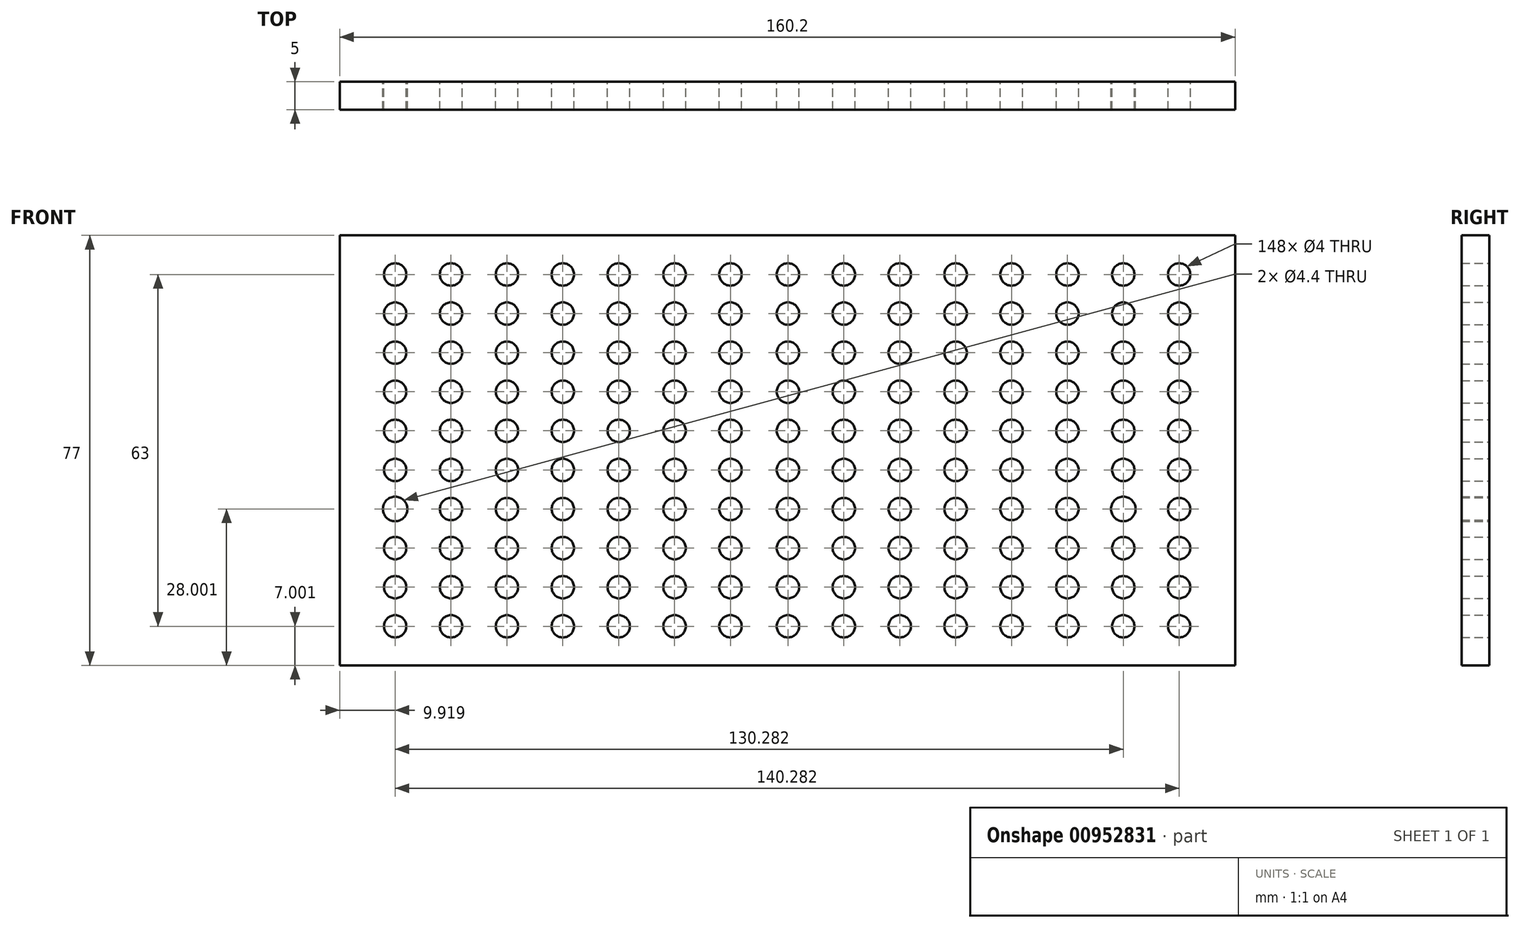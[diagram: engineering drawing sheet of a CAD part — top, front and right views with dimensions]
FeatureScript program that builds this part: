
annotation { "Feature Type Name" : "Feature", "Feature Type Description" : "" }
export const myFeature = defineFeature(function(context is Context, id is Id, definition is map)
    precondition{}
    {
        {
            var Q0;
            Q0=qCreatedBy(makeId("Front.planeOp"),FACE);
            var sketch = newSketch(context, id + "F0", { "sketchPlane" : qUnion([Q0])});
            skLineSegment(sketch, "E0.bottom", {"start": v(-75.06, 32.6) * mm, "end": v(85.14, 32.6) * mm});
            skLineSegment(sketch, "E0.top", {"start": v(-75.06, -44.4) * mm, "end": v(85.14, -44.4) * mm});
            skLineSegment(sketch, "E0.left", {"start": v(-75.06, 32.6) * mm, "end": v(-75.06, -44.4) * mm});
            skLineSegment(sketch, "E0.right", {"start": v(85.14, 32.6) * mm, "end": v(85.14, -44.4) * mm});
            skCircle(sketch, "E1", {"center": v(75.14, 18.6) * mm, "radius": 2 * mm});
            skCircle(sketch, "E2", {"center": v(75.14, 11.6) * mm, "radius": 2 * mm});
            skCircle(sketch, "E3", {"center": v(75.14, 4.6) * mm, "radius": 2 * mm});
            skCircle(sketch, "E4", {"center": v(75.14, -2.4) * mm, "radius": 2 * mm});
            skCircle(sketch, "E5", {"center": v(75.14, -9.4) * mm, "radius": 2 * mm});
            skCircle(sketch, "E6", {"center": v(75.14, -16.4) * mm, "radius": 2 * mm});
            skCircle(sketch, "E7", {"center": v(75.14, -23.4) * mm, "radius": 2 * mm});
            skCircle(sketch, "E8", {"center": v(75.14, -30.4) * mm, "radius": 2 * mm});
            skCircle(sketch, "E9", {"center": v(75.14, -37.4) * mm, "radius": 2 * mm});
            skCircle(sketch, "E10", {"center": v(75.14, 25.6) * mm, "radius": 2 * mm});
            skCircle(sketch, "E11.MirrorC", {"center": v(65.14, 25.6) * mm, "radius": 2 * mm});
            skCircle(sketch, "E12.MirrorC", {"center": v(65.14, 18.6) * mm, "radius": 2 * mm});
            skCircle(sketch, "E13.MirrorC", {"center": v(65.14, 11.6) * mm, "radius": 2 * mm});
            skCircle(sketch, "E14.MirrorC", {"center": v(65.14, 4.6) * mm, "radius": 2 * mm});
            skCircle(sketch, "E15.MirrorC", {"center": v(65.14, -2.4) * mm, "radius": 2 * mm});
            skCircle(sketch, "E16.MirrorC", {"center": v(65.14, -9.4) * mm, "radius": 2 * mm});
            skCircle(sketch, "E17.MirrorC", {"center": v(65.14, -16.4) * mm, "radius": 2.2 * mm});
            skCircle(sketch, "E18.MirrorC", {"center": v(65.14, -23.4) * mm, "radius": 2 * mm});
            skCircle(sketch, "E19.MirrorC", {"center": v(65.14, -30.4) * mm, "radius": 2 * mm});
            skCircle(sketch, "E20.MirrorC", {"center": v(65.14, -37.4) * mm, "radius": 2 * mm});
            skCircle(sketch, "E21.MirrorC", {"center": v(55.14, 25.6) * mm, "radius": 2 * mm});
            skCircle(sketch, "E22.MirrorC", {"center": v(45.14, 25.6) * mm, "radius": 2 * mm});
            skCircle(sketch, "E23.MirrorC", {"center": v(55.14, 18.6) * mm, "radius": 2 * mm});
            skCircle(sketch, "E24.MirrorC", {"center": v(45.14, 18.6) * mm, "radius": 2 * mm});
            skCircle(sketch, "E25.MirrorC", {"center": v(45.14, 11.6) * mm, "radius": 2 * mm});
            skCircle(sketch, "E26.MirrorC", {"center": v(55.14, 4.6) * mm, "radius": 2 * mm});
            skCircle(sketch, "E27.MirrorC", {"center": v(55.14, 11.6) * mm, "radius": 2 * mm});
            skCircle(sketch, "E28.MirrorC", {"center": v(45.14, 4.6) * mm, "radius": 2 * mm});
            skCircle(sketch, "E29.MirrorC", {"center": v(55.14, -2.4) * mm, "radius": 2 * mm});
            skCircle(sketch, "E30.MirrorC", {"center": v(45.14, -2.4) * mm, "radius": 2 * mm});
            skCircle(sketch, "E31.MirrorC", {"center": v(55.14, -9.4) * mm, "radius": 2 * mm});
            skCircle(sketch, "E32.MirrorC", {"center": v(45.14, -16.4) * mm, "radius": 2 * mm});
            skCircle(sketch, "E33.MirrorC", {"center": v(55.14, -16.4) * mm, "radius": 2 * mm});
            skCircle(sketch, "E34.MirrorC", {"center": v(55.14, -23.4) * mm, "radius": 2 * mm});
            skCircle(sketch, "E35.MirrorC", {"center": v(45.14, -23.4) * mm, "radius": 2 * mm});
            skCircle(sketch, "E36.MirrorC", {"center": v(45.14, -30.4) * mm, "radius": 2 * mm});
            skCircle(sketch, "E37.MirrorC", {"center": v(55.14, -30.4) * mm, "radius": 2 * mm});
            skCircle(sketch, "E38.MirrorC", {"center": v(55.14, -37.4) * mm, "radius": 2 * mm});
            skCircle(sketch, "E39.MirrorC", {"center": v(45.14, -37.4) * mm, "radius": 2 * mm});
            skCircle(sketch, "E40.MirrorC", {"center": v(45.14, -9.4) * mm, "radius": 2 * mm});
            skCircle(sketch, "E41.MirrorC", {"center": v(35.14, 25.6) * mm, "radius": 2 * mm});
            skCircle(sketch, "E42.MirrorC", {"center": v(25.14, 25.6) * mm, "radius": 2 * mm});
            skCircle(sketch, "E43.MirrorC", {"center": v(15.14, 25.6) * mm, "radius": 2 * mm});
            skCircle(sketch, "E44.MirrorC", {"center": v(5.14, 25.6) * mm, "radius": 2 * mm});
            skCircle(sketch, "E45.MirrorC", {"center": v(5.14, 18.6) * mm, "radius": 2 * mm});
            skCircle(sketch, "E46.MirrorC", {"center": v(15.14, 18.6) * mm, "radius": 2 * mm});
            skCircle(sketch, "E47.MirrorC", {"center": v(25.14, 18.6) * mm, "radius": 2 * mm});
            skCircle(sketch, "E48.MirrorC", {"center": v(35.14, 18.6) * mm, "radius": 2 * mm});
            skCircle(sketch, "E49.MirrorC", {"center": v(35.14, 11.6) * mm, "radius": 2 * mm});
            skCircle(sketch, "E50.MirrorC", {"center": v(25.14, 11.6) * mm, "radius": 2 * mm});
            skCircle(sketch, "E51.MirrorC", {"center": v(15.14, 11.6) * mm, "radius": 2 * mm});
            skCircle(sketch, "E52.MirrorC", {"center": v(5.14, 11.6) * mm, "radius": 2 * mm});
            skCircle(sketch, "E53.MirrorC", {"center": v(5.14, 4.6) * mm, "radius": 2 * mm});
            skCircle(sketch, "E54.MirrorC", {"center": v(15.14, 4.6) * mm, "radius": 2 * mm});
            skCircle(sketch, "E55.MirrorC", {"center": v(25.14, 4.6) * mm, "radius": 2 * mm});
            skCircle(sketch, "E56.MirrorC", {"center": v(35.14, 4.6) * mm, "radius": 2 * mm});
            skCircle(sketch, "E57.MirrorC", {"center": v(35.14, -2.4) * mm, "radius": 2 * mm});
            skCircle(sketch, "E58.MirrorC", {"center": v(25.14, -2.4) * mm, "radius": 2 * mm});
            skCircle(sketch, "E59.MirrorC", {"center": v(15.14, -2.4) * mm, "radius": 2 * mm});
            skCircle(sketch, "E60.MirrorC", {"center": v(5.14, -2.4) * mm, "radius": 2 * mm});
            skCircle(sketch, "E61.MirrorC", {"center": v(5.14, -9.4) * mm, "radius": 2 * mm});
            skCircle(sketch, "E62.MirrorC", {"center": v(15.14, -9.4) * mm, "radius": 2 * mm});
            skCircle(sketch, "E63.MirrorC", {"center": v(25.14, -9.4) * mm, "radius": 2 * mm});
            skCircle(sketch, "E64.MirrorC", {"center": v(35.14, -9.4) * mm, "radius": 2 * mm});
            skCircle(sketch, "E65.MirrorC", {"center": v(35.14, -16.4) * mm, "radius": 2 * mm});
            skCircle(sketch, "E66.MirrorC", {"center": v(25.14, -16.4) * mm, "radius": 2 * mm});
            skCircle(sketch, "E67.MirrorC", {"center": v(15.14, -16.4) * mm, "radius": 2 * mm});
            skCircle(sketch, "E68.MirrorC", {"center": v(5.14, -16.4) * mm, "radius": 2 * mm});
            skCircle(sketch, "E69.MirrorC", {"center": v(5.14, -23.4) * mm, "radius": 2 * mm});
            skCircle(sketch, "E70.MirrorC", {"center": v(15.14, -23.4) * mm, "radius": 2 * mm});
            skCircle(sketch, "E71.MirrorC", {"center": v(25.14, -23.4) * mm, "radius": 2 * mm});
            skCircle(sketch, "E72.MirrorC", {"center": v(35.14, -23.4) * mm, "radius": 2 * mm});
            skCircle(sketch, "E73.MirrorC", {"center": v(35.14, -30.4) * mm, "radius": 2 * mm});
            skCircle(sketch, "E74.MirrorC", {"center": v(25.14, -30.4) * mm, "radius": 2 * mm});
            skCircle(sketch, "E75.MirrorC", {"center": v(15.14, -30.4) * mm, "radius": 2 * mm});
            skCircle(sketch, "E76.MirrorC", {"center": v(5.14, -30.4) * mm, "radius": 2 * mm});
            skCircle(sketch, "E77.MirrorC", {"center": v(35.14, -37.4) * mm, "radius": 2 * mm});
            skCircle(sketch, "E78.MirrorC", {"center": v(25.14, -37.4) * mm, "radius": 2 * mm});
            skCircle(sketch, "E79.MirrorC", {"center": v(15.14, -37.4) * mm, "radius": 2 * mm});
            skCircle(sketch, "E80.MirrorC", {"center": v(5.14, -37.4) * mm, "radius": 2 * mm});
            skCircle(sketch, "E81.MirrorC", {"center": v(-5.14, 18.6) * mm, "radius": 2 * mm});
            skCircle(sketch, "E82.MirrorC", {"center": v(-15.14, 18.6) * mm, "radius": 2 * mm});
            skCircle(sketch, "E83.MirrorC", {"center": v(-25.14, 18.6) * mm, "radius": 2 * mm});
            skCircle(sketch, "E84.MirrorC", {"center": v(-35.14, 18.6) * mm, "radius": 2 * mm});
            skCircle(sketch, "E85.MirrorC", {"center": v(-45.14, 18.6) * mm, "radius": 2 * mm});
            skCircle(sketch, "E86.MirrorC", {"center": v(-55.14, 18.6) * mm, "radius": 2 * mm});
            skCircle(sketch, "E87.MirrorC", {"center": v(-65.14, 18.6) * mm, "radius": 2 * mm});
            skCircle(sketch, "E88.MirrorC", {"center": v(-5.14, 25.6) * mm, "radius": 2 * mm});
            skCircle(sketch, "E89.MirrorC", {"center": v(-15.14, 25.6) * mm, "radius": 2 * mm});
            skCircle(sketch, "E90.MirrorC", {"center": v(-25.14, 25.6) * mm, "radius": 2 * mm});
            skCircle(sketch, "E91.MirrorC", {"center": v(-35.14, 25.6) * mm, "radius": 2 * mm});
            skCircle(sketch, "E92.MirrorC", {"center": v(-45.14, 25.6) * mm, "radius": 2 * mm});
            skCircle(sketch, "E93.MirrorC", {"center": v(-55.14, 25.6) * mm, "radius": 2 * mm});
            skCircle(sketch, "E94.MirrorC", {"center": v(-65.14, 25.6) * mm, "radius": 2 * mm});
            skCircle(sketch, "E95.MirrorC", {"center": v(-5.14, 11.6) * mm, "radius": 2 * mm});
            skCircle(sketch, "E96.MirrorC", {"center": v(-15.14, 11.6) * mm, "radius": 2 * mm});
            skCircle(sketch, "E97.MirrorC", {"center": v(-25.14, 11.6) * mm, "radius": 2 * mm});
            skCircle(sketch, "E98.MirrorC", {"center": v(-35.14, 11.6) * mm, "radius": 2 * mm});
            skCircle(sketch, "E99.MirrorC", {"center": v(-45.14, 11.6) * mm, "radius": 2 * mm});
            skCircle(sketch, "E100.MirrorC", {"center": v(-55.14, 11.6) * mm, "radius": 2 * mm});
            skCircle(sketch, "E101.MirrorC", {"center": v(-65.14, 11.6) * mm, "radius": 2 * mm});
            skCircle(sketch, "E102.MirrorC", {"center": v(-65.14, 4.6) * mm, "radius": 2 * mm});
            skCircle(sketch, "E103.MirrorC", {"center": v(-55.14, 4.6) * mm, "radius": 2 * mm});
            skCircle(sketch, "E104.MirrorC", {"center": v(-45.14, 4.6) * mm, "radius": 2 * mm});
            skCircle(sketch, "E105.MirrorC", {"center": v(-35.14, 4.6) * mm, "radius": 2 * mm});
            skCircle(sketch, "E106.MirrorC", {"center": v(-25.14, 4.6) * mm, "radius": 2 * mm});
            skCircle(sketch, "E107.MirrorC", {"center": v(-15.14, 4.6) * mm, "radius": 2 * mm});
            skCircle(sketch, "E108.MirrorC", {"center": v(-5.14, 4.6) * mm, "radius": 2 * mm});
            skCircle(sketch, "E109.MirrorC", {"center": v(-5.14, -2.4) * mm, "radius": 2 * mm});
            skCircle(sketch, "E110.MirrorC", {"center": v(-15.14, -2.4) * mm, "radius": 2 * mm});
            skCircle(sketch, "E111.MirrorC", {"center": v(-25.14, -2.4) * mm, "radius": 2 * mm});
            skCircle(sketch, "E112.MirrorC", {"center": v(-35.14, -2.4) * mm, "radius": 2 * mm});
            skCircle(sketch, "E113.MirrorC", {"center": v(-45.14, -2.4) * mm, "radius": 2 * mm});
            skCircle(sketch, "E114.MirrorC", {"center": v(-55.14, -2.4) * mm, "radius": 2 * mm});
            skCircle(sketch, "E115.MirrorC", {"center": v(-65.14, -2.4) * mm, "radius": 2 * mm});
            skCircle(sketch, "E116.MirrorC", {"center": v(-65.14, -9.4) * mm, "radius": 2 * mm});
            skCircle(sketch, "E117.MirrorC", {"center": v(-55.14, -9.4) * mm, "radius": 2 * mm});
            skCircle(sketch, "E118.MirrorC", {"center": v(-45.14, -9.4) * mm, "radius": 2 * mm});
            skCircle(sketch, "E119.MirrorC", {"center": v(-35.14, -9.4) * mm, "radius": 2 * mm});
            skCircle(sketch, "E120.MirrorC", {"center": v(-25.14, -9.4) * mm, "radius": 2 * mm});
            skCircle(sketch, "E121.MirrorC", {"center": v(-15.14, -9.4) * mm, "radius": 2 * mm});
            skCircle(sketch, "E122.MirrorC", {"center": v(-5.14, -9.4) * mm, "radius": 2 * mm});
            skCircle(sketch, "E123.MirrorC", {"center": v(-5.14, -16.4) * mm, "radius": 2 * mm});
            skCircle(sketch, "E124.MirrorC", {"center": v(-15.14, -16.4) * mm, "radius": 2 * mm});
            skCircle(sketch, "E125.MirrorC", {"center": v(-25.14, -16.4) * mm, "radius": 2 * mm});
            skCircle(sketch, "E126.MirrorC", {"center": v(-35.14, -16.4) * mm, "radius": 2 * mm});
            skCircle(sketch, "E127.MirrorC", {"center": v(-45.14, -16.4) * mm, "radius": 2 * mm});
            skCircle(sketch, "E128.MirrorC", {"center": v(-55.14, -16.4) * mm, "radius": 2 * mm});
            skCircle(sketch, "E129.MirrorC", {"center": v(-65.14, -16.4) * mm, "radius": 2.2 * mm});
            skCircle(sketch, "E130.MirrorC", {"center": v(-65.14, -23.4) * mm, "radius": 2 * mm});
            skCircle(sketch, "E131.MirrorC", {"center": v(-55.14, -23.4) * mm, "radius": 2 * mm});
            skCircle(sketch, "E132.MirrorC", {"center": v(-45.14, -23.4) * mm, "radius": 2 * mm});
            skCircle(sketch, "E133.MirrorC", {"center": v(-35.14, -23.4) * mm, "radius": 2 * mm});
            skCircle(sketch, "E134.MirrorC", {"center": v(-25.14, -23.4) * mm, "radius": 2 * mm});
            skCircle(sketch, "E135.MirrorC", {"center": v(-15.14, -23.4) * mm, "radius": 2 * mm});
            skCircle(sketch, "E136.MirrorC", {"center": v(-5.14, -23.4) * mm, "radius": 2 * mm});
            skCircle(sketch, "E137.MirrorC", {"center": v(-5.14, -30.4) * mm, "radius": 2 * mm});
            skCircle(sketch, "E138.MirrorC", {"center": v(-15.14, -30.4) * mm, "radius": 2 * mm});
            skCircle(sketch, "E139.MirrorC", {"center": v(-25.14, -30.4) * mm, "radius": 2 * mm});
            skCircle(sketch, "E140.MirrorC", {"center": v(-35.14, -30.4) * mm, "radius": 2 * mm});
            skCircle(sketch, "E141.MirrorC", {"center": v(-45.14, -30.4) * mm, "radius": 2 * mm});
            skCircle(sketch, "E142.MirrorC", {"center": v(-55.14, -30.4) * mm, "radius": 2 * mm});
            skCircle(sketch, "E143.MirrorC", {"center": v(-65.14, -30.4) * mm, "radius": 2 * mm});
            skCircle(sketch, "E144.MirrorC", {"center": v(-5.14, -37.4) * mm, "radius": 2 * mm});
            skCircle(sketch, "E145.MirrorC", {"center": v(-15.14, -37.4) * mm, "radius": 2 * mm});
            skCircle(sketch, "E146.MirrorC", {"center": v(-25.14, -37.4) * mm, "radius": 2 * mm});
            skCircle(sketch, "E147.MirrorC", {"center": v(-35.14, -37.4) * mm, "radius": 2 * mm});
            skCircle(sketch, "E148.MirrorC", {"center": v(-45.14, -37.4) * mm, "radius": 2 * mm});
            skCircle(sketch, "E149.MirrorC", {"center": v(-55.14, -37.4) * mm, "radius": 2 * mm});
            skCircle(sketch, "E150.MirrorC", {"center": v(-65.14, -37.4) * mm, "radius": 2 * mm});
            skSolve(sketch);
        }
        {
            var Q0;
            Q0=makeQuery(id+"F0.imprint","IMPRINT",FACE,{"disambiguationData":[TD([[makeQuery(id+"F0.imprint","IMPRINT",EDGE,{"derivedFrom":sQuery(id+"F0.wireOp",EDGE,"E0.bottom")}),-1.0]])]});
            extrude(context, id + "F1", {"entities" : qUnion([Q0]), "depth" : 5 * mm, "offsetDistance" : 25.4 * mm});
        }
    });
